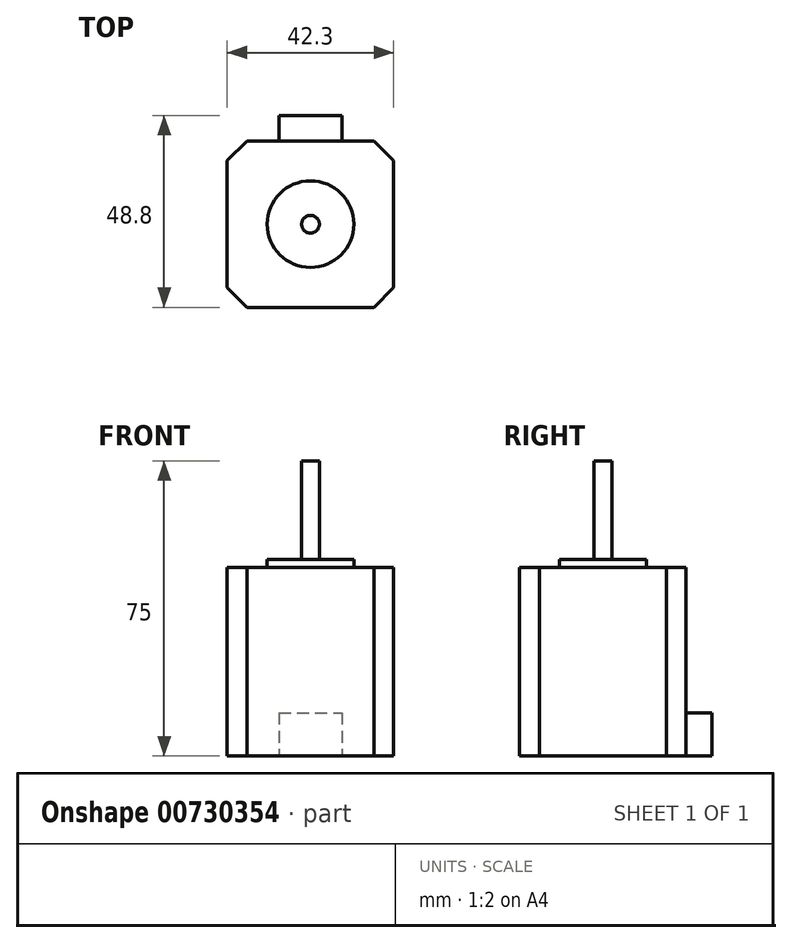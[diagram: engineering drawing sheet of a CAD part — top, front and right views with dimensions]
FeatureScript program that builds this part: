
annotation { "Feature Type Name" : "Feature", "Feature Type Description" : "" }
export const myFeature = defineFeature(function(context is Context, id is Id, definition is map)
    precondition{}
    {
        {
            var Q0;
            Q0=qCreatedBy(makeId("Top.planeOp"),FACE);
            var sketch = newSketch(context, id + "F0", { "sketchPlane" : qUnion([Q0])});
            skLineSegment(sketch, "E0.bottom", {"start": v(-16.15, 21.15) * mm, "end": v(16.15, 21.15) * mm});
            skLineSegment(sketch, "E0.top", {"start": v(-16.15, -21.15) * mm, "end": v(16.15, -21.15) * mm});
            skLineSegment(sketch, "E0.left", {"start": v(-21.15, 16.15) * mm, "end": v(-21.15, -16.15) * mm});
            skLineSegment(sketch, "E0.right", {"start": v(21.15, 16.15) * mm, "end": v(21.15, -16.15) * mm});
            skPoint(sketch, "E1", {"position": v(-15.5, 15.5) * mm});
            skPoint(sketch, "E2", {"position": v(15.5, 15.5) * mm});
            skPoint(sketch, "E3", {"position": v(15.5, -15.5) * mm});
            skPoint(sketch, "E4", {"position": v(-15.5, -15.5) * mm});
            skLineSegment(sketch, "E5", {"start": v(-21.15, 16.15) * mm, "end": v(-16.15, 21.15) * mm});
            skLineSegment(sketch, "E6.MirrorCS", {"start": v(21.15, 16.15) * mm, "end": v(16.15, 21.15) * mm});
            skLineSegment(sketch, "E7.MirrorCS", {"start": v(-21.15, -16.15) * mm, "end": v(-16.15, -21.15) * mm});
            skLineSegment(sketch, "E8.MirrorCS", {"start": v(21.15, -16.15) * mm, "end": v(16.15, -21.15) * mm});
            skSolve(sketch);
        }
        {
            var Q0;
            Q0=makeQuery(id+"F0.imprint","IMPRINT",FACE,{"disambiguationData":[TD([[makeQuery(id+"F0.imprint","IMPRINT",EDGE,{"derivedFrom":sQuery(id+"F0.wireOp",EDGE,"E0.bottom")}),-1.0]])]});
            extrude(context, id + "F1", {"entities" : qUnion([Q0]), "depth" : 48 * mm, "offsetDistance" : 25 * mm});
        }
        {
            var Q0;
            Q0=qCreatedBy(makeId("Top.planeOp"),FACE);
            var sketch = newSketch(context, id + "F2", { "sketchPlane" : qUnion([Q0])});
            skLineSegment(sketch, "E9.bottom", {"start": v(-8, 21.15) * mm, "end": v(8, 21.15) * mm});
            skLineSegment(sketch, "E9.top", {"start": v(-8, 27.65) * mm, "end": v(8, 27.65) * mm});
            skLineSegment(sketch, "E9.left", {"start": v(-8, 21.15) * mm, "end": v(-8, 27.65) * mm});
            skLineSegment(sketch, "E9.right", {"start": v(8, 21.15) * mm, "end": v(8, 27.65) * mm});
            skSolve(sketch);
        }
        {
            var Q0;
            Q0=makeQuery(id+"F2.imprint","IMPRINT",FACE,{"disambiguationData":[TD([[makeQuery(id+"F2.imprint","IMPRINT",EDGE,{"derivedFrom":sQuery(id+"F2.wireOp",EDGE,"E9.bottom")}),1.0]])]});
            extrude(context, id + "F3", {"entities" : qUnion([Q0]), "operationType" : NewBodyOperationType.ADD, "depth" : 11 * mm, "offsetDistance" : 25 * mm});
        }
        {
            var Q0;
            Q0=makeQuery(id+"F1.opExtrude","CAP_FACE",FACE,{"disambiguationData":[OSD([sQuery(id+"F0.wireOp",EDGE,"E0.bottom"),sQuery(id+"F0.wireOp",EDGE,"E0.top"),sQuery(id+"F0.wireOp",EDGE,"E0.left"),sQuery(id+"F0.wireOp",EDGE,"E0.right"),sQuery(id+"F0.wireOp",EDGE,"E5"),sQuery(id+"F0.wireOp",EDGE,"E6.MirrorCS"),sQuery(id+"F0.wireOp",EDGE,"E7.MirrorCS"),sQuery(id+"F0.wireOp",EDGE,"E8.MirrorCS")])],"isStart":false});
            var sketch = newSketch(context, id + "F4", { "sketchPlane" : qUnion([Q0])});
            skCircle(sketch, "E10", {"center": v(0, 0) * mm, "radius": 11 * mm});
            skSolve(sketch);
        }
        {
            var Q0;
            Q0=makeQuery(id+"F4.imprint","IMPRINT",FACE,{"disambiguationData":[TD([[makeQuery(id+"F4.imprint","IMPRINT",EDGE,{"derivedFrom":sQuery(id+"F4.wireOp",EDGE,"E10")}),1.0]])]});
            extrude(context, id + "F5", {"entities" : qUnion([Q0]), "operationType" : NewBodyOperationType.ADD, "depth" : 2 * mm, "offsetDistance" : 25 * mm});
        }
        {
            var Q0;
            Q0=makeQuery(id+"F5.opExtrude","CAP_FACE",FACE,{"disambiguationData":[OSD([sQuery(id+"F4.wireOp",EDGE,"E10")])],"isStart":false});
            var sketch = newSketch(context, id + "F6", { "sketchPlane" : qUnion([Q0])});
            skCircle(sketch, "E11", {"center": v(0, 0) * mm, "radius": 2.25 * mm});
            skSolve(sketch);
        }
        {
            var Q0;
            Q0=makeQuery(id+"F6.imprint","IMPRINT",FACE,{"disambiguationData":[TD([[makeQuery(id+"F6.imprint","IMPRINT",EDGE,{"derivedFrom":sQuery(id+"F6.wireOp",EDGE,"E11")}),1.0]])]});
            extrude(context, id + "F7", {"entities" : qUnion([Q0]), "operationType" : NewBodyOperationType.ADD, "depth" : 25 * mm, "offsetDistance" : 25 * mm});
        }
    });
